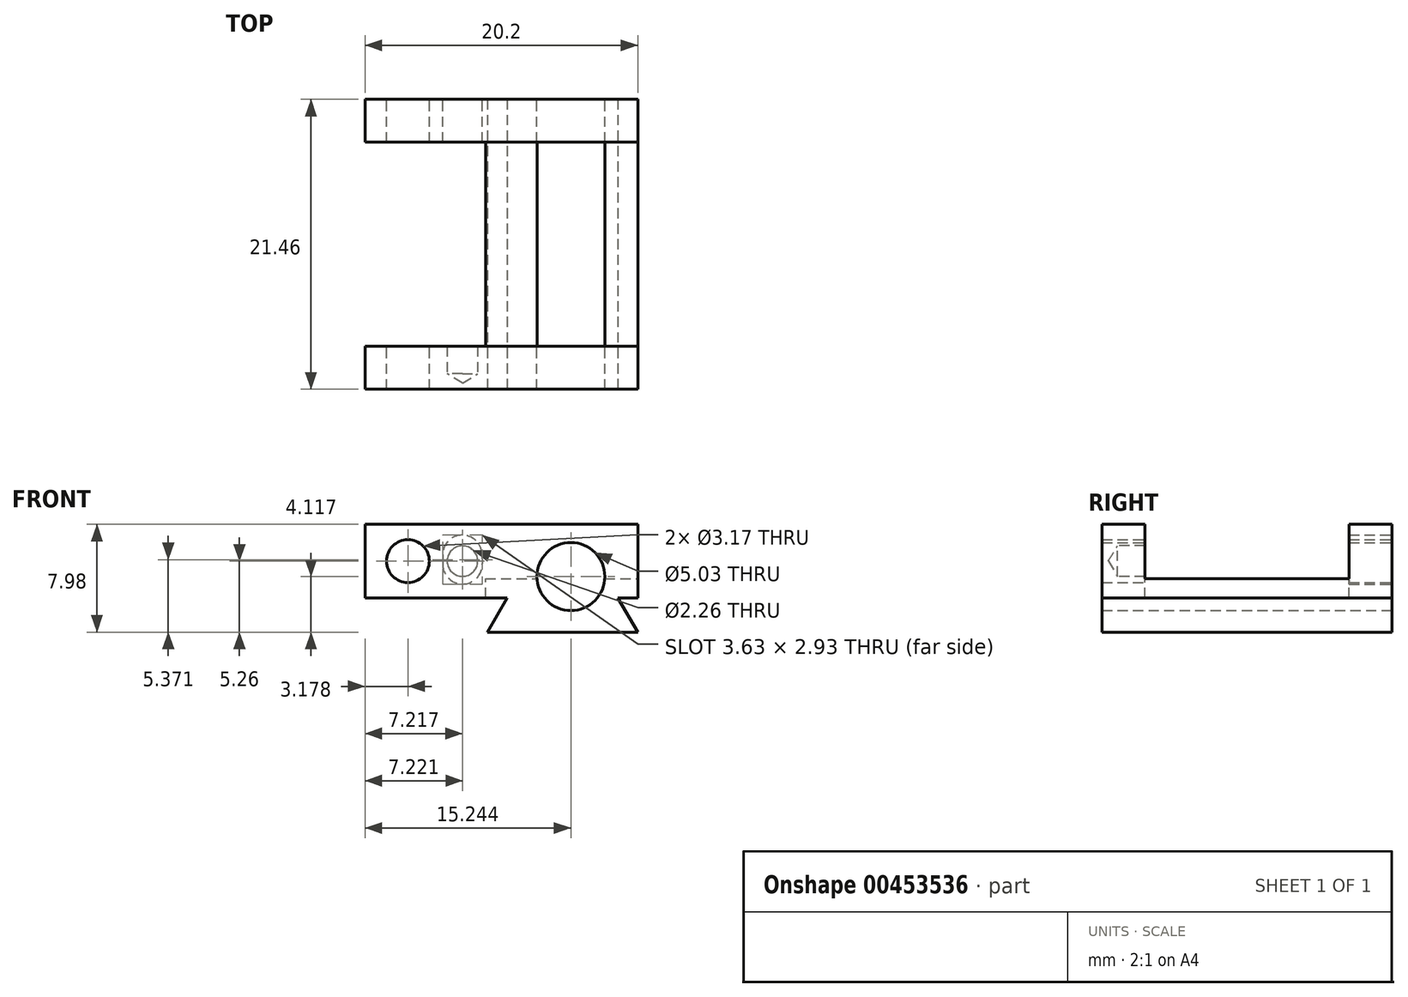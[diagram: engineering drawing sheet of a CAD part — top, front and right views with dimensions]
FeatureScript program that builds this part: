
annotation { "Feature Type Name" : "Feature", "Feature Type Description" : "" }
export const myFeature = defineFeature(function(context is Context, id is Id, definition is map)
    precondition{}
    {
        {
            var Q0;
            Q0=qCreatedBy(makeId("Front.planeOp"),FACE);
            var sketch = newSketch(context, id + "F0", { "sketchPlane" : qUnion([Q0]), "disableImprinting" : false});
            skLineSegment(sketch, "E0.bottom", {"start": v(-10.1, 3.99) * mm, "end": v(10.1, 3.99) * mm});
            skLineSegment(sketch, "E0.top", {"start": v(-10.1, -3.99) * mm, "end": v(10.1, -3.99) * mm});
            skLineSegment(sketch, "E0.left", {"start": v(-10.1, 3.99) * mm, "end": v(-10.1, -3.99) * mm});
            skLineSegment(sketch, "E0.right", {"start": v(10.1, 3.99) * mm, "end": v(10.1, -3.99) * mm});
            skLineSegment(sketch, "E1", {"start": v(-10.1, -3.99) * mm, "end": v(10.1, 3.99) * mm, "construction": true});
            skLineSegment(sketch, "E2", {"start": v(-10.1, 3.99) * mm, "end": v(10.1, -3.99) * mm, "construction": true});
            skSolve(sketch);
        }
        {
            var Q0;
            Q0=makeQuery(id+"F0.imprint","IMPRINT",FACE,{"disambiguationData":[TD([[makeQuery(id+"F0.imprint","IMPRINT",EDGE,{"derivedFrom":sQuery(id+"F0.wireOp",EDGE,"E0.bottom")}),-1.0]])]});
            extrude(context, id + "F1", {"entities" : qUnion([Q0]), "depth" : 21.46 * mm, "symmetric" : true});
        }
        {
            var Q0;
            Q0=makeQuery(id+"F1.opExtrude","CAP_FACE",FACE,{"disambiguationData":[OSD([sQuery(id+"F0.wireOp",EDGE,"E0.bottom"),sQuery(id+"F0.wireOp",EDGE,"E0.top"),sQuery(id+"F0.wireOp",EDGE,"E0.left"),sQuery(id+"F0.wireOp",EDGE,"E0.right")])],"isStart":false});
            var sketch = newSketch(context, id + "F2", { "sketchPlane" : qUnion([Q0]), "disableImprinting" : false});
            skLineSegment(sketch, "E3.bottom", {"start": v(-10.1, -1.45) * mm, "end": v(0.44, -1.45) * mm});
            skLineSegment(sketch, "E3.right", {"start": v(10.1, -1.45) * mm, "end": v(10.1, -3.99) * mm});
            skLineSegment(sketch, "E4", {"start": v(10.1, -3.99) * mm, "end": v(8.63, -1.45) * mm});
            skLineSegment(sketch, "E5", {"start": v(-1.03, -3.99) * mm, "end": v(0.44, -1.45) * mm});
            skLineSegment(sketch, "E6.0", {"start": v(-10.1, -3.99) * mm, "end": v(10.1, -3.99) * mm});
            skLineSegment(sketch, "E7.0", {"start": v(-10.1, 3.99) * mm, "end": v(-10.1, -3.99) * mm});
            skLineSegment(sketch, "E8", {"start": v(0.44, -1.45) * mm, "end": v(8.63, -1.45) * mm, "construction": true});
            skLineSegment(sketch, "E9", {"start": v(8.63, -1.45) * mm, "end": v(10.1, -1.45) * mm});
            skLineSegment(sketch, "E10", {"start": v(-1.03, -3.99) * mm, "end": v(-10.1, -3.99) * mm});
            skLineSegment(sketch, "E11", {"start": v(-10.1, -3.99) * mm, "end": v(-10.1, -1.45) * mm});
            skSolve(sketch);
        }
        {
            var Q0;
            Q0=makeQuery(id+"F2.imprint","IMPRINT",FACE,{"disambiguationData":[TD([[makeQuery(id+"F2.imprint","IMPRINT",EDGE,{"derivedFrom":sQuery(id+"F2.wireOp",EDGE,"E3.bottom")}),-1.0]])]});
            var Q1;
            Q1=makeQuery(id+"F2.imprint","IMPRINT",FACE,{"disambiguationData":[TD([[makeQuery(id+"F2.imprint","IMPRINT",EDGE,{"derivedFrom":sQuery(id+"F2.wireOp",EDGE,"E3.right")}),-1.0]])]});
            extrude(context, id + "F3", {"entities" : qUnion([Q0, Q1]), "operationType" : NewBodyOperationType.REMOVE, "endBound" : BoundingType.THROUGH_ALL, "oppositeDirection" : true, "depth" : 25.4 * mm});
        }
        {
            var Q0;
            Q0=makeQuery(id+"F1.opExtrude","CAP_FACE",FACE,{"disambiguationData":[OSD([sQuery(id+"F0.wireOp",EDGE,"E0.bottom"),sQuery(id+"F0.wireOp",EDGE,"E0.top"),sQuery(id+"F0.wireOp",EDGE,"E0.left"),sQuery(id+"F0.wireOp",EDGE,"E0.right")])],"isStart":false});
            var sketch = newSketch(context, id + "F4", { "sketchPlane" : qUnion([Q0]), "disableImprinting" : false});
            skPoint(sketch, "E12", {"position": v(5.14, 0.13) * mm});
            skSolve(sketch);
        }
        {
            var Q0;
            Q0=sQuery(id+"F4.wireOp",VERTEX,"E12");
            var Q1;
            Q1=makeQuery(id+"F1.opExtrude","SWEPT_BODY",BODY,{"disambiguationData":[OSD([sQuery(id+"F0.wireOp",EDGE,"E0.bottom"),sQuery(id+"F0.wireOp",EDGE,"E0.top"),sQuery(id+"F0.wireOp",EDGE,"E0.left"),sQuery(id+"F0.wireOp",EDGE,"E0.right")])]});
            hole(context, id + "F5", {"style" : HoleStyle.SIMPLE, "endStyle" : HoleEndStyle.THROUGH, "holeDiameter" : 5.03 * mm, "isTappedThrough" : true, "tappedDepth" : 5.7 * mm, "tapClearance" : 3, "locations" : qUnion([Q0]), "scope" : qUnion([Q1]), "startStyle" : HoleStartStyle.SKETCH});
        }
        {
            var Q0;
            Q0=makeQuery(id+"F1.opExtrude","SWEPT_FACE",FACE,{"disambiguationData":[OSD([sQuery(id+"F0.wireOp",EDGE,"E0.right")])]});
            var sketch = newSketch(context, id + "F6", { "sketchPlane" : qUnion([Q0])});
            skLineSegment(sketch, "E13.bottom", {"start": v(-7.56, 3.99) * mm, "end": v(7.56, 3.99) * mm});
            skLineSegment(sketch, "E13.top", {"start": v(-7.56, -0.02) * mm, "end": v(7.56, -0.02) * mm});
            skLineSegment(sketch, "E13.left", {"start": v(-7.56, 3.99) * mm, "end": v(-7.56, -0.02) * mm});
            skLineSegment(sketch, "E13.right", {"start": v(7.56, 3.99) * mm, "end": v(7.56, -0.02) * mm});
            skSolve(sketch);
        }
        {
            var Q0;
            Q0=makeQuery(id+"F6.imprint","IMPRINT",FACE,{"disambiguationData":[TD([[makeQuery(id+"F6.imprint","IMPRINT",EDGE,{"derivedFrom":sQuery(id+"F6.wireOp",EDGE,"E13.bottom")}),-1.0]])]});
            extrude(context, id + "F7", {"entities" : qUnion([Q0]), "operationType" : NewBodyOperationType.REMOVE, "oppositeDirection" : true, "depth" : 15.88 * mm});
        }
        {
            var Q0;
            Q0=makeQuery(id+"F1.opExtrude","CAP_FACE",FACE,{"disambiguationData":[OSD([sQuery(id+"F0.wireOp",EDGE,"E0.bottom"),sQuery(id+"F0.wireOp",EDGE,"E0.top"),sQuery(id+"F0.wireOp",EDGE,"E0.left"),sQuery(id+"F0.wireOp",EDGE,"E0.right")])],"isStart":false});
            var sketch = newSketch(context, id + "F8", { "sketchPlane" : qUnion([Q0]), "disableImprinting" : false});
            skPoint(sketch, "E14", {"position": v(-6.92, 1.27) * mm});
            skSolve(sketch);
        }
        {
            var Q0;
            Q0=sQuery(id+"F8.wireOp",VERTEX,"E14");
            var Q1;
            Q1=makeQuery(id+"F1.opExtrude","SWEPT_BODY",BODY,{"disambiguationData":[OSD([sQuery(id+"F0.wireOp",EDGE,"E0.bottom"),sQuery(id+"F0.wireOp",EDGE,"E0.top"),sQuery(id+"F0.wireOp",EDGE,"E0.left"),sQuery(id+"F0.wireOp",EDGE,"E0.right")])]});
            hole(context, id + "F9", {"style" : HoleStyle.SIMPLE, "endStyle" : HoleEndStyle.THROUGH, "holeDiameter" : 3.17 * mm, "isTappedThrough" : true, "tappedDepth" : 5.7 * mm, "tapClearance" : 3, "locations" : qUnion([Q0]), "scope" : qUnion([Q1]), "startStyle" : HoleStartStyle.SKETCH});
        }
        {
            var Q0;
            Q0=makeQuery(id+"F1.opExtrude","CAP_FACE",FACE,{"disambiguationData":[OSD([sQuery(id+"F0.wireOp",EDGE,"E0.bottom"),sQuery(id+"F0.wireOp",EDGE,"E0.top"),sQuery(id+"F0.wireOp",EDGE,"E0.left"),sQuery(id+"F0.wireOp",EDGE,"E0.right")])],"isStart":true});
            var sketch = newSketch(context, id + "F10", { "sketchPlane" : qUnion([Q0]), "disableImprinting" : false});
            skPoint(sketch, "E15", {"position": v(2.88, 1.27) * mm});
            skSolve(sketch);
        }
        {
            var Q0;
            Q0=sQuery(id+"F10.wireOp",VERTEX,"E15");
            var Q1;
            Q1=makeQuery(id+"F1.opExtrude","SWEPT_BODY",BODY,{"disambiguationData":[OSD([sQuery(id+"F0.wireOp",EDGE,"E0.bottom"),sQuery(id+"F0.wireOp",EDGE,"E0.top"),sQuery(id+"F0.wireOp",EDGE,"E0.left"),sQuery(id+"F0.wireOp",EDGE,"E0.right")])]});
            hole(context, id + "F11", {"style" : HoleStyle.SIMPLE, "endStyle" : HoleEndStyle.BLIND, "standardTappedOrClearance" : lookupTablePath({ "standard" : "ANSI", "engagement" : "75%", "pitch" : "40 tpi", "size" : "#4", "type" : "Tapped" }), "standardBlindInLast" : lookupTablePath({ "standard" : "ANSI", "engagement" : "75%", "pitch" : "40 tpi", "size" : "#4", "type" : "Tapped" }), "holeDiameter" : 2.26 * mm, "showTappedDepth" : true, "holeDepth" : 20.32 * mm, "isTappedThrough" : true, "tappedDepth" : 18.41 * mm, "tapClearance" : 3, "locations" : qUnion([Q0]), "scope" : qUnion([Q1]), "majorDiameter" : 2.84 * mm, "startStyle" : HoleStartStyle.SKETCH});
        }
        {
            var Q0;
            Q0=makeQuery(id+"F1.opExtrude","SWEPT_FACE",FACE,{"disambiguationData":[OSD([sQuery(id+"F0.wireOp",EDGE,"E0.bottom")])]});
            var sketch = newSketch(context, id + "F12", { "sketchPlane" : qUnion([Q0])});
            skLineSegment(sketch, "E16.bottom", {"start": v(-10.1, -7.56) * mm, "end": v(-1.18, -7.56) * mm});
            skLineSegment(sketch, "E16.top", {"start": v(-10.1, 7.56) * mm, "end": v(-1.18, 7.56) * mm});
            skLineSegment(sketch, "E16.left", {"start": v(-10.1, -7.56) * mm, "end": v(-10.1, 7.56) * mm});
            skLineSegment(sketch, "E16.right", {"start": v(-1.18, -7.56) * mm, "end": v(-1.18, 7.56) * mm});
            skSolve(sketch);
        }
        {
            var Q0;
            {var subQ2=sQuery(id+"F12.wireOp",EDGE,"E16.left");Q0=makeQuery(id+"F12.imprint","IMPRINT",FACE,{"disambiguationData":[TD([[makeQuery(id+"F12.imprint","IMPRINT",EDGE,{"derivedFrom":subQ2}),-1.0]])]});}
            var Q1;
            {var subQ3=sQuery(id+"F12.wireOp",EDGE,"E16.right");Q1=makeQuery(id+"F12.imprint","IMPRINT",FACE,{"disambiguationData":[TD([[makeQuery(id+"F12.imprint","IMPRINT",EDGE,{"derivedFrom":subQ3}),1.0]])]});}
            extrude(context, id + "F13", {"entities" : qUnion([Q0, Q1]), "operationType" : NewBodyOperationType.REMOVE, "endBound" : BoundingType.THROUGH_ALL, "oppositeDirection" : true, "depth" : 25.4 * mm});
        }
        {
            var Q0;
            Q0=makeQuery(id+"F1.opExtrude","CAP_FACE",FACE,{"disambiguationData":[OSD([sQuery(id+"F0.wireOp",EDGE,"E0.bottom"),sQuery(id+"F0.wireOp",EDGE,"E0.top"),sQuery(id+"F0.wireOp",EDGE,"E0.left"),sQuery(id+"F0.wireOp",EDGE,"E0.right")])],"isStart":true});
            var sketch = newSketch(context, id + "F14", { "sketchPlane" : qUnion([Q0]), "disableImprinting" : false});
            skCircle(sketch, "E17.0", {"center": v(6.92, 1.27) * mm, "radius": 1.59 * mm});
            skArc(sketch, "E18", {"start": v(4.35, 1.74) * mm, "mid": v(2.92, 3.2) * mm, "end": v(1.44, 1.79) * mm});
            skArc(sketch, "E19", {"start": v(1.41, 1.08) * mm, "mid": v(2.85, -0.43) * mm, "end": v(4.35, 1.03) * mm});
            skLineSegment(sketch, "E20", {"start": v(1.44, 1.79) * mm, "end": v(1.41, 1.08) * mm});
            skLineSegment(sketch, "E21", {"start": v(4.35, 1.74) * mm, "end": v(4.35, 1.03) * mm});
            skLineSegment(sketch, "E22", {"start": v(2.9, 1.74) * mm, "end": v(2.88, 1.03) * mm, "construction": true});
            skSolve(sketch);
        }
        {
            var Q0;
            Q0=makeQuery(id+"F14.imprint","IMPRINT",FACE,{"disambiguationData":[TD([[makeQuery(id+"F14.imprint","IMPRINT",EDGE,{"derivedFrom":sQuery(id+"F14.wireOp",EDGE,"E18")}),1.0]])]});
            extrude(context, id + "F15", {"entities" : qUnion([Q0]), "operationType" : NewBodyOperationType.REMOVE, "endBound" : BoundingType.UP_TO_NEXT, "oppositeDirection" : true, "depth" : 25.4 * mm});
        }
    });
